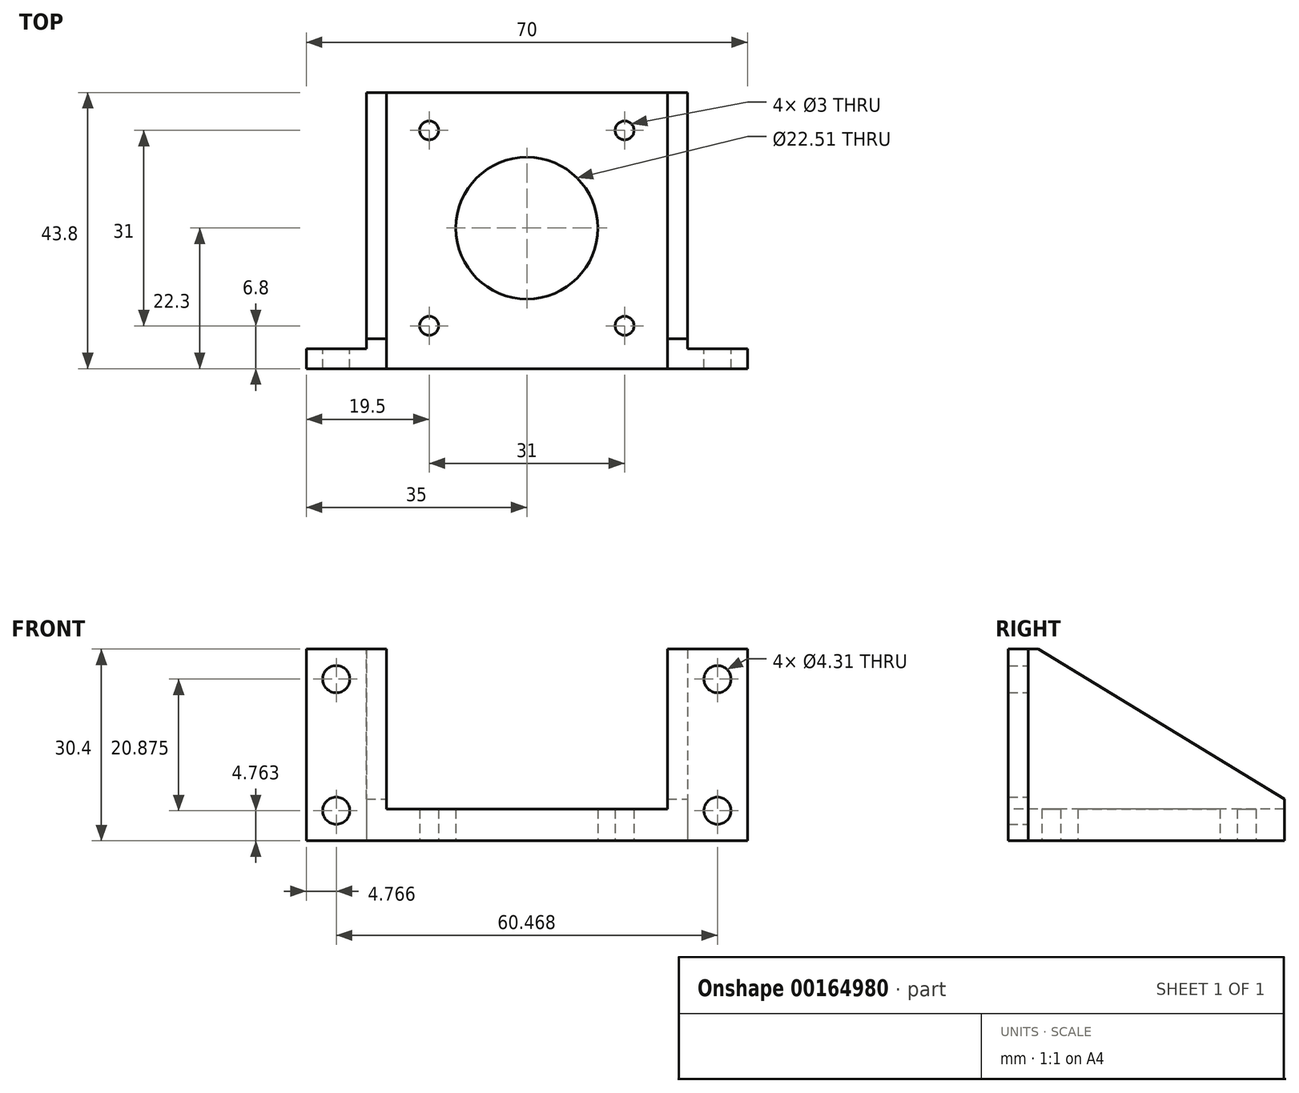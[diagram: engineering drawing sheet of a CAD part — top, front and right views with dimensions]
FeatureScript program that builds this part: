
annotation { "Feature Type Name" : "Feature", "Feature Type Description" : "" }
export const myFeature = defineFeature(function(context is Context, id is Id, definition is map)
    precondition{}
    {
        {
            var Q0;
            Q0=qCreatedBy(makeId("Top.planeOp"),FACE);
            var sketch = newSketch(context, id + "F0", { "sketchPlane" : qUnion([Q0])});
            skLineSegment(sketch, "E0.bottom", {"start": v(15.5, 15.5) * mm, "end": v(-15.5, 15.5) * mm, "construction": true});
            skLineSegment(sketch, "E0.top", {"start": v(15.5, -15.5) * mm, "end": v(-15.5, -15.5) * mm, "construction": true});
            skLineSegment(sketch, "E0.left", {"start": v(15.5, 15.5) * mm, "end": v(15.5, -15.5) * mm, "construction": true});
            skLineSegment(sketch, "E0.right", {"start": v(-15.5, 15.5) * mm, "end": v(-15.5, -15.5) * mm, "construction": true});
            skPoint(sketch, "E0.middle", {"position": v(0, 0) * mm});
            skCircle(sketch, "E1", {"center": v(15.5, 15.5) * mm, "radius": 1.5 * mm});
            skCircle(sketch, "E2", {"center": v(15.5, -15.5) * mm, "radius": 1.5 * mm});
            skCircle(sketch, "E3", {"center": v(-15.5, -15.5) * mm, "radius": 1.5 * mm});
            skCircle(sketch, "E4", {"center": v(-15.5, 15.5) * mm, "radius": 1.5 * mm});
            skCircle(sketch, "E5", {"center": v(0, 0) * mm, "radius": 11.25 * mm});
            skLineSegment(sketch, "E6.bottom", {"start": v(-25.47, 21.5) * mm, "end": v(25.47, 21.5) * mm});
            skLineSegment(sketch, "E6.top", {"start": v(-35, -22.3) * mm, "end": v(35, -22.3) * mm});
            skLineSegment(sketch, "E6.left", {"start": v(-25.47, 21.5) * mm, "end": v(-25.47, -19.12) * mm});
            skLineSegment(sketch, "E6.right", {"start": v(25.47, 21.5) * mm, "end": v(25.47, -19.12) * mm});
            skLineSegment(sketch, "E7", {"start": v(0, 0) * mm, "end": v(25.47, 0) * mm, "construction": true});
            skLineSegment(sketch, "E8", {"start": v(0, 0) * mm, "end": v(0, -22.3) * mm, "construction": true});
            skLineSegment(sketch, "E9", {"start": v(0, 0) * mm, "end": v(-25.47, 0) * mm, "construction": true});
            skLineSegment(sketch, "E10", {"start": v(0, 0) * mm, "end": v(0, 21.5) * mm, "construction": true});
            skLineSegment(sketch, "E11.bottom", {"start": v(25.47, -19.12) * mm, "end": v(35, -19.12) * mm});
            skLineSegment(sketch, "E11.right", {"start": v(35, -19.12) * mm, "end": v(35, -22.3) * mm});
            skLineSegment(sketch, "E12", {"start": v(-35, -22.3) * mm, "end": v(-35, -19.12) * mm});
            skLineSegment(sketch, "E13", {"start": v(-35, -19.12) * mm, "end": v(-25.47, -19.12) * mm});
            skSolve(sketch);
        }
        {
            var Q0;
            Q0 = qSketchRegion(id + "F0", true);
            extrude(context, id + "F1", {"entities" : qUnion([Q0]), "depth" : 5 * mm});
        }
        {
            var Q0;
            Q0=makeQuery(id+"F1.opExtrude","CAP_FACE",FACE,{"disambiguationData":[OSD([sQuery(id+"F0.wireOp",EDGE,"E1"),sQuery(id+"F0.wireOp",EDGE,"E2"),sQuery(id+"F0.wireOp",EDGE,"E3"),sQuery(id+"F0.wireOp",EDGE,"E4"),sQuery(id+"F0.wireOp",EDGE,"E5"),sQuery(id+"F0.wireOp",EDGE,"E6.bottom"),sQuery(id+"F0.wireOp",EDGE,"E6.top"),sQuery(id+"F0.wireOp",EDGE,"E6.left"),sQuery(id+"F0.wireOp",EDGE,"E6.right"),sQuery(id+"F0.wireOp",EDGE,"E11.bottom"),sQuery(id+"F0.wireOp",EDGE,"E11.right"),sQuery(id+"F0.wireOp",EDGE,"E12"),sQuery(id+"F0.wireOp",EDGE,"E13")])],"isStart":false});
            var sketch = newSketch(context, id + "F2", { "sketchPlane" : qUnion([Q0])});
            skLineSegment(sketch, "E14.top", {"start": v(-35, -22.3) * mm, "end": v(-22.3, -22.3) * mm});
            skLineSegment(sketch, "E14.left", {"start": v(-35, -19.12) * mm, "end": v(-35, -22.3) * mm});
            skLineSegment(sketch, "E15.top", {"start": v(-22.3, 21.5) * mm, "end": v(-25.47, 21.5) * mm});
            skLineSegment(sketch, "E15.left", {"start": v(-22.3, -22.3) * mm, "end": v(-22.3, 21.5) * mm});
            skLineSegment(sketch, "E15.right", {"start": v(-25.47, -19.12) * mm, "end": v(-25.47, 21.5) * mm});
            skLineSegment(sketch, "E16", {"start": v(-35, -19.12) * mm, "end": v(-25.47, -19.12) * mm});
            skLineSegment(sketch, "E17.bottom", {"start": v(25.47, 21.5) * mm, "end": v(22.3, 21.5) * mm});
            skLineSegment(sketch, "E17.left", {"start": v(25.47, 21.5) * mm, "end": v(25.47, -19.12) * mm});
            skLineSegment(sketch, "E17.right", {"start": v(22.3, 21.5) * mm, "end": v(22.3, -22.3) * mm});
            skLineSegment(sketch, "E18.bottom", {"start": v(25.47, -19.12) * mm, "end": v(35, -19.12) * mm});
            skLineSegment(sketch, "E18.top", {"start": v(22.3, -22.3) * mm, "end": v(35, -22.3) * mm});
            skLineSegment(sketch, "E18.right", {"start": v(35, -19.12) * mm, "end": v(35, -22.3) * mm});
            skSolve(sketch);
        }
        {
            var Q0;
            Q0 = qSketchRegion(id + "F2", true);
            extrude(context, id + "F3", {"entities" : qUnion([Q0]), "operationType" : NewBodyOperationType.ADD, "depth" : 25.4 * mm});
        }
        {
            var Q0;
            Q0=makeQuery(id+"F3.boolean.opBoolean","MERGE",FACE,{"derivedFrom":[makeQuery(id+"F1.opExtrude","SWEPT_FACE",FACE,{"disambiguationData":[OSD([sQuery(id+"F0.wireOp",EDGE,"E11.bottom")])]}),makeQuery(id+"F3.opExtrude","SWEPT_FACE",FACE,{"disambiguationData":[OSD([sQuery(id+"F2.wireOp",EDGE,"E18.bottom")])]})]});
            var sketch = newSketch(context, id + "F4", { "sketchPlane" : qUnion([Q0])});
            skLineSegment(sketch, "E19.bottom", {"start": v(30.23, 0) * mm, "end": v(35, 0) * mm, "construction": true});
            skLineSegment(sketch, "E19.top", {"start": v(30.23, 4.76) * mm, "end": v(35, 4.76) * mm, "construction": true});
            skLineSegment(sketch, "E19.left", {"start": v(30.23, 0) * mm, "end": v(30.23, 4.76) * mm, "construction": true});
            skLineSegment(sketch, "E19.right", {"start": v(35, 0) * mm, "end": v(35, 4.76) * mm, "construction": true});
            skLineSegment(sketch, "E20.bottom", {"start": v(30.23, 30.4) * mm, "end": v(35, 30.4) * mm, "construction": true});
            skLineSegment(sketch, "E20.top", {"start": v(30.23, 25.64) * mm, "end": v(35, 25.64) * mm, "construction": true});
            skLineSegment(sketch, "E20.left", {"start": v(30.23, 30.4) * mm, "end": v(30.23, 25.64) * mm, "construction": true});
            skLineSegment(sketch, "E20.right", {"start": v(35, 30.4) * mm, "end": v(35, 25.64) * mm, "construction": true});
            skLineSegment(sketch, "E21.bottom", {"start": v(-30.23, 0) * mm, "end": v(-35, 0) * mm, "construction": true});
            skLineSegment(sketch, "E21.top", {"start": v(-30.23, 4.76) * mm, "end": v(-35, 4.76) * mm, "construction": true});
            skLineSegment(sketch, "E21.left", {"start": v(-30.23, 0) * mm, "end": v(-30.23, 4.76) * mm, "construction": true});
            skLineSegment(sketch, "E21.right", {"start": v(-35, 0) * mm, "end": v(-35, 4.76) * mm, "construction": true});
            skLineSegment(sketch, "E22.bottom", {"start": v(-30.23, 30.4) * mm, "end": v(-35, 30.4) * mm, "construction": true});
            skLineSegment(sketch, "E22.top", {"start": v(-30.23, 25.64) * mm, "end": v(-35, 25.64) * mm, "construction": true});
            skLineSegment(sketch, "E22.left", {"start": v(-30.23, 30.4) * mm, "end": v(-30.23, 25.64) * mm, "construction": true});
            skLineSegment(sketch, "E22.right", {"start": v(-35, 30.4) * mm, "end": v(-35, 25.64) * mm, "construction": true});
            skCircle(sketch, "E23", {"center": v(30.23, 4.76) * mm, "radius": 2.15 * mm});
            skCircle(sketch, "E24", {"center": v(30.23, 25.64) * mm, "radius": 2.15 * mm});
            skCircle(sketch, "E25", {"center": v(-30.23, 25.64) * mm, "radius": 2.15 * mm});
            skCircle(sketch, "E26", {"center": v(-30.23, 4.76) * mm, "radius": 2.15 * mm});
            skSolve(sketch);
        }
        {
            var Q0;
            Q0 = qSketchRegion(id + "F4", true);
            var Q1;
            Q1=makeQuery(id+"F3.boolean.opBoolean","MERGE",FACE,{"derivedFrom":[makeQuery(id+"F1.opExtrude","SWEPT_FACE",FACE,{"disambiguationData":[OSD([sQuery(id+"F0.wireOp",EDGE,"E6.top")])]}),makeQuery(id+"F3.opExtrude","SWEPT_FACE",FACE,{"disambiguationData":[OSD([sQuery(id+"F2.wireOp",EDGE,"E14.top")])]}),makeQuery(id+"F3.opExtrude","SWEPT_FACE",FACE,{"disambiguationData":[OSD([sQuery(id+"F2.wireOp",EDGE,"E18.top")])]})]});
            extrude(context, id + "F5", {"entities" : qUnion([Q0]), "operationType" : NewBodyOperationType.REMOVE, "endBound" : BoundingType.UP_TO_SURFACE, "oppositeDirection" : true, "endBoundEntityFace" : qUnion([Q1]), "depth" : 25.4 * mm});
        }
        {
            var Q0;
            Q0=makeQuery(id+"F3.boolean.opBoolean","MERGE",FACE,{"derivedFrom":[makeQuery(id+"F1.opExtrude","SWEPT_FACE",FACE,{"disambiguationData":[OSD([sQuery(id+"F0.wireOp",EDGE,"E6.right")])]}),makeQuery(id+"F3.opExtrude","SWEPT_FACE",FACE,{"disambiguationData":[OSD([sQuery(id+"F2.wireOp",EDGE,"E17.left")])]})]});
            var sketch = newSketch(context, id + "F6", { "sketchPlane" : qUnion([Q0])});
            skLineSegment(sketch, "E27.bottom", {"start": v(21.5, 30.4) * mm, "end": v(-17.53, 30.4) * mm});
            skLineSegment(sketch, "E27.top", {"start": v(21.5, 6.59) * mm, "end": v(-17.53, 6.59) * mm, "construction": true});
            skLineSegment(sketch, "E27.left", {"start": v(21.5, 30.4) * mm, "end": v(21.5, 6.59) * mm});
            skLineSegment(sketch, "E27.right", {"start": v(-17.53, 30.4) * mm, "end": v(-17.53, 6.59) * mm, "construction": true});
            skLineSegment(sketch, "E28", {"start": v(-17.53, 30.4) * mm, "end": v(21.5, 6.59) * mm});
            skLineSegment(sketch, "E29", {"start": v(21.5, 6.59) * mm, "end": v(21.5, 5) * mm, "construction": true});
            skLineSegment(sketch, "E30", {"start": v(-17.53, 30.4) * mm, "end": v(-19.12, 30.4) * mm, "construction": true});
            skSolve(sketch);
        }
        {
            var Q0;
            Q0 = qSketchRegion(id + "F6", true);
            var Q1;
            Q1=makeQuery(id+"F3.boolean.opBoolean","MERGE",FACE,{"derivedFrom":[makeQuery(id+"F1.opExtrude","SWEPT_FACE",FACE,{"disambiguationData":[OSD([sQuery(id+"F0.wireOp",EDGE,"E6.left")])]}),makeQuery(id+"F3.opExtrude","SWEPT_FACE",FACE,{"disambiguationData":[OSD([sQuery(id+"F2.wireOp",EDGE,"E15.right")])]})]});
            extrude(context, id + "F7", {"entities" : qUnion([Q0]), "operationType" : NewBodyOperationType.REMOVE, "endBound" : BoundingType.UP_TO_SURFACE, "oppositeDirection" : true, "endBoundEntityFace" : qUnion([Q1]), "depth" : 25.4 * mm});
        }
    });
